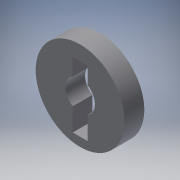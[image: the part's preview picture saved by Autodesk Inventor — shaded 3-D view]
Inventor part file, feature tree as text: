
AUTODESK INVENTOR PART (.ipt)
format: ipt  version: 2017 (Build 210142000, 142)  size: 114,688 bytes
history: native  units: in
note: dims shown in document units (in); Inventor stores cm internally (conversion verified against a paired STEP export)
features: sketch x4, extrude x3
ambient origin geometry x8: Origin, YZ Plane, XZ Plane, XY Plane, X Axis, Y Axis, Z Axis, Center Point
bodies: Solid1 (feature_tree)
feature tree (7):
  sketch  "Sketch1"  dims[d0=1.7717in d1=0.3937in d2=0.0in]
  extrude  "Extrusion1"  Depth=0.3937in TaperAngle=0.0deg
  extrude  "Extrusion2"  Depth=0.2953in
  extrude  "Extrusion3"  Depth=0.5906in
  sketch  "Sketch2"  dims[d3=0.2953in d4=1.6929in]
  sketch  "Sketch3"  dims[d6=0.1476in d7=0.5906in]
  sketch  "Sketch4"  dims[d8=0.3937in d9=0.0in d10=0.5906in d11=0.3937in d12=0.0in]
